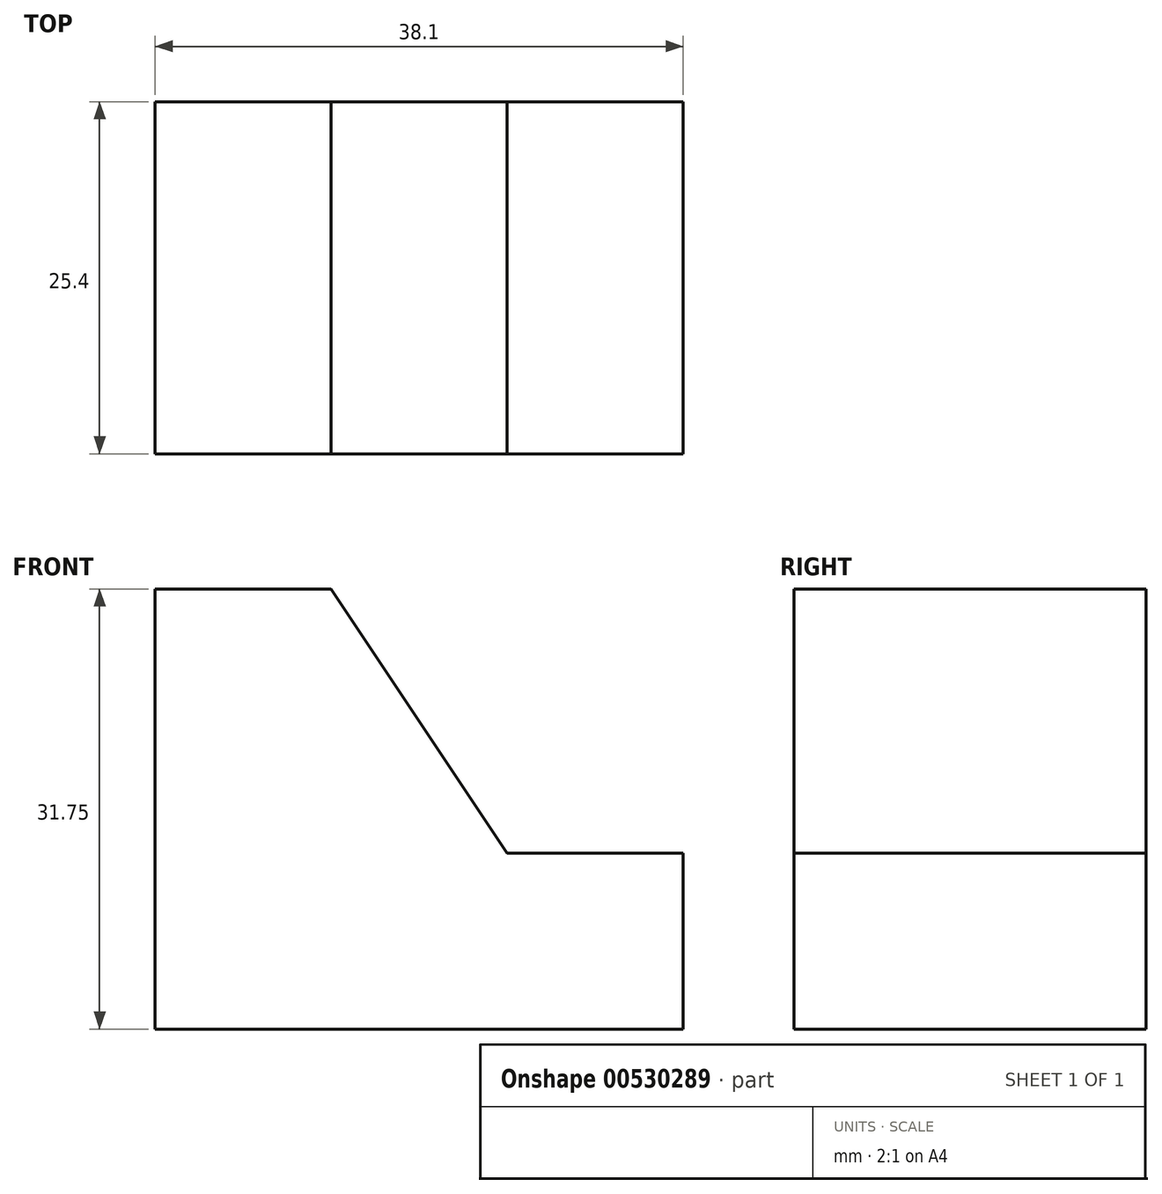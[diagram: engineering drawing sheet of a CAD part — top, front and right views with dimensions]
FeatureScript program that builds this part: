
annotation { "Feature Type Name" : "Feature", "Feature Type Description" : "" }
export const myFeature = defineFeature(function(context is Context, id is Id, definition is map)
    precondition{}
    {
        {
            var Q0;
            Q0=qCreatedBy(makeId("Front.planeOp"),FACE);
            var sketch = newSketch(context, id + "F0", { "sketchPlane" : qUnion([Q0])});
            skLineSegment(sketch, "E0", {"start": v(-51.5, 31.75) * mm, "end": v(-51.5, 0) * mm});
            skLineSegment(sketch, "E1", {"start": v(-51.5, 0) * mm, "end": v(-13.4, 0) * mm});
            skLineSegment(sketch, "E2", {"start": v(-51.5, 31.75) * mm, "end": v(-38.8, 31.75) * mm});
            skLineSegment(sketch, "E3", {"start": v(-13.4, 0) * mm, "end": v(-13.4, 12.7) * mm});
            skLineSegment(sketch, "E4", {"start": v(-13.4, 12.7) * mm, "end": v(-26.1, 12.7) * mm});
            skLineSegment(sketch, "E5", {"start": v(-38.8, 31.75) * mm, "end": v(-26.1, 12.7) * mm});
            skSolve(sketch);
        }
        {
            var Q0;
            Q0=makeQuery(id+"F0.imprint","IMPRINT",FACE,{"disambiguationData":[TD([[makeQuery(id+"F0.imprint","IMPRINT",EDGE,{"derivedFrom":sQuery(id+"F0.wireOp",EDGE,"E0")}),1.0]])]});
            extrude(context, id + "F1", {"entities" : qUnion([Q0]), "depth" : 25.4 * mm, "offsetDistance" : 25.4 * mm});
        }
    });
